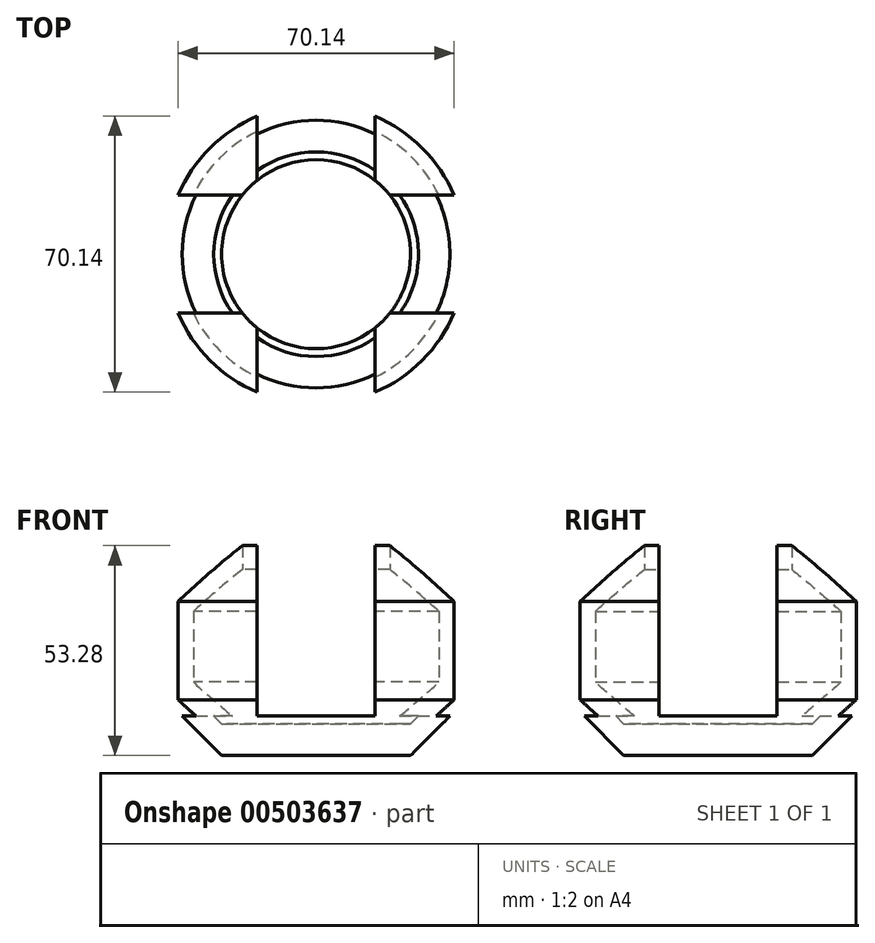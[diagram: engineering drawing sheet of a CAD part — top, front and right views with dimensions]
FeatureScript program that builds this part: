
annotation { "Feature Type Name" : "Feature", "Feature Type Description" : "" }
export const myFeature = defineFeature(function(context is Context, id is Id, definition is map)
    precondition{}
    {
        {
            var Q0;
            Q0=qCreatedBy(makeId("Top.planeOp"),FACE);
            var sketch = newSketch(context, id + "F0", { "sketchPlane" : qUnion([Q0])});
            skCircle(sketch, "E0", {"center": v(0, 0) * mm, "radius": 24 * mm});
            skCircle(sketch, "E1", {"center": v(0, 0) * mm, "radius": 23 * mm});
            skSolve(sketch);
        }
        {
            var Q0;
            Q0=makeQuery(id+"F0.imprint","IMPRINT",FACE,{"disambiguationData":[TD([[makeQuery(id+"F0.imprint","IMPRINT",EDGE,{"derivedFrom":sQuery(id+"F0.wireOp",EDGE,"E0")}),1.0]])]});
            extrude(context, id + "F1", {"entities" : qUnion([Q0]), "depth" : 8 * mm});
        }
        {
            var Q0;
            Q0=makeQuery(id+"F0.imprint","IMPRINT",FACE,{"disambiguationData":[TD([[makeQuery(id+"F0.imprint","IMPRINT",EDGE,{"derivedFrom":sQuery(id+"F0.wireOp",EDGE,"E1")}),1.0]])]});
            extrude(context, id + "F2", {"entities" : qUnion([Q0]), "operationType" : NewBodyOperationType.ADD, "depth" : 2 * mm});
        }
        {
            var Q0;
            Q0=qCreatedBy(makeId("Right.planeOp"),FACE);
            var sketch = newSketch(context, id + "F3", { "sketchPlane" : qUnion([Q0])});
            skLineSegment(sketch, "E2", {"start": v(0, 0) * mm, "end": v(0, 55) * mm});
            skLineSegment(sketch, "E3.0", {"start": v(-24, 0) * mm, "end": v(24, 0) * mm});
            skLineSegment(sketch, "E4.0", {"start": v(-24, 8) * mm, "end": v(24, 8) * mm});
            skLineSegment(sketch, "E5", {"start": v(24, 0) * mm, "end": v(38.14, 14.14) * mm});
            skLineSegment(sketch, "E6", {"start": v(24, 8) * mm, "end": v(34.6, 18.6) * mm});
            skLineSegment(sketch, "E7", {"start": v(38.14, 14.14) * mm, "end": v(38.14, 39.14) * mm});
            skLineSegment(sketch, "E8", {"start": v(34.6, 18.6) * mm, "end": v(34.6, 36.6) * mm});
            skLineSegment(sketch, "E9", {"start": v(38.14, 39.14) * mm, "end": v(24, 53.28) * mm});
            skLineSegment(sketch, "E10", {"start": v(34.6, 36.6) * mm, "end": v(24, 47.21) * mm});
            skLineSegment(sketch, "E11", {"start": v(0, 55) * mm, "end": v(75.35, 55) * mm});
            skLineSegment(sketch, "E12", {"start": v(24, 0) * mm, "end": v(24, 55) * mm});
            skLineSegment(sketch, "E13", {"start": v(24, 53.28) * mm, "end": v(24, 47.21) * mm});
            skSolve(sketch);
        }
        {
            var Q0;
            {var subQ0=sQuery(id+"F3.wireOp",EDGE,"E3.0");var subQ1=sQuery(id+"F3.wireOp",EDGE,"E2");var subQ2=makeQuery(id+"F3.imprint","INTERSECT",VERTEX,{"derivedFrom":[subQ1,subQ0]});Q0=makeQuery(id+"F3.imprint","IMPRINT",FACE,{"disambiguationData":[TD([[makeQuery(id+"F3.imprint","IMPRINT",EDGE,{"disambiguationData":[TD([[subQ2,-1.0]])],"derivedFrom":subQ1}),-1.0]])]});}
            var Q1;
            {var subQ1=sQuery(id+"F3.wireOp",EDGE,"E5");Q1=makeQuery(id+"F3.imprint","IMPRINT",FACE,{"disambiguationData":[TD([[makeQuery(id+"F3.imprint","IMPRINT",EDGE,{"derivedFrom":subQ1}),1.0]])]});}
            var Q2;
            Q2=sQuery(id+"F3.wireOp",EDGE,"E2");
            revolve(context, id + "F4", {"operationType" : NewBodyOperationType.ADD, "entities" : qUnion([Q0, Q1]), "axis" : qUnion([Q2]), "revolveType" : RevolveType.FULL});
        }
        {
            var Q0;
            Q0=qCreatedBy(makeId("Right.planeOp"),FACE);
            var sketch = newSketch(context, id + "F5", { "sketchPlane" : qUnion([Q0])});
            skLineSegment(sketch, "E14", {"start": v(0, 10) * mm, "end": v(0, 152.7) * mm});
            skLineSegment(sketch, "E15", {"start": v(0, 0) * mm, "end": v(15, 0) * mm});
            skLineSegment(sketch, "E16", {"start": v(15, 10) * mm, "end": v(15, 85) * mm});
            skLineSegment(sketch, "E17", {"start": v(15, 153.21) * mm, "end": v(0, 152.7) * mm});
            skLineSegment(sketch, "E18", {"start": v(0, 10) * mm, "end": v(15, 10) * mm});
            skLineSegment(sketch, "E19.MirrorCS", {"start": v(0, 10) * mm, "end": v(-15, 10) * mm});
            skLineSegment(sketch, "E20.MirrorCS", {"start": v(-15, 10) * mm, "end": v(-15, 85) * mm});
            skPoint(sketch, "E21.orphan", {"position": v(-15, 0) * mm});
            skLineSegment(sketch, "E22.trimOffspring", {"start": v(15, 94.51) * mm, "end": v(15, 153.21) * mm});
            skPoint(sketch, "E23.orphan", {"position": v(-15, 153.21) * mm});
            skPoint(sketch, "E24.start.orphan", {"position": v(0, 84.51) * mm});
            skLineSegment(sketch, "E25", {"start": v(-15, 85) * mm, "end": v(15, 85) * mm});
            skLineSegment(sketch, "E26", {"start": v(-15, 10) * mm, "end": v(15, 10) * mm});
            skSolve(sketch);
        }
        {
            var Q0;
            Q0 = qSketchRegion(id + "F5", true);
            extrude(context, id + "F6", {"entities" : qUnion([Q0]), "operationType" : NewBodyOperationType.REMOVE, "endBound" : BoundingType.SYMMETRIC, "oppositeDirection" : true, "depth" : 150 * mm});
        }
        {
            var Q0;
            Q0=qCreatedBy(makeId("Front.planeOp"),FACE);
            var sketch = newSketch(context, id + "F7", { "sketchPlane" : qUnion([Q0])});
            skLineSegment(sketch, "E27", {"start": v(0, 0) * mm, "end": v(15, 0) * mm});
            skLineSegment(sketch, "E28", {"start": v(15, 10) * mm, "end": v(0, 10) * mm});
            skLineSegment(sketch, "E29", {"start": v(0, 10) * mm, "end": v(0, 85) * mm});
            skLineSegment(sketch, "E30", {"start": v(0, 85) * mm, "end": v(15, 85) * mm});
            skLineSegment(sketch, "E31", {"start": v(15, 85) * mm, "end": v(15, 10) * mm});
            skLineSegment(sketch, "E32.MirrorCS", {"start": v(0, 85) * mm, "end": v(-15, 85) * mm});
            skLineSegment(sketch, "E33.MirrorCS", {"start": v(-15, 85) * mm, "end": v(-15, 10) * mm});
            skLineSegment(sketch, "E34.MirrorCS", {"start": v(-15, 10) * mm, "end": v(0, 10) * mm});
            skSolve(sketch);
        }
        {
            var Q0;
            Q0 = qSketchRegion(id + "F7", true);
            extrude(context, id + "F8", {"entities" : qUnion([Q0]), "operationType" : NewBodyOperationType.REMOVE, "endBound" : BoundingType.SYMMETRIC, "depth" : 150 * mm});
        }
    });
